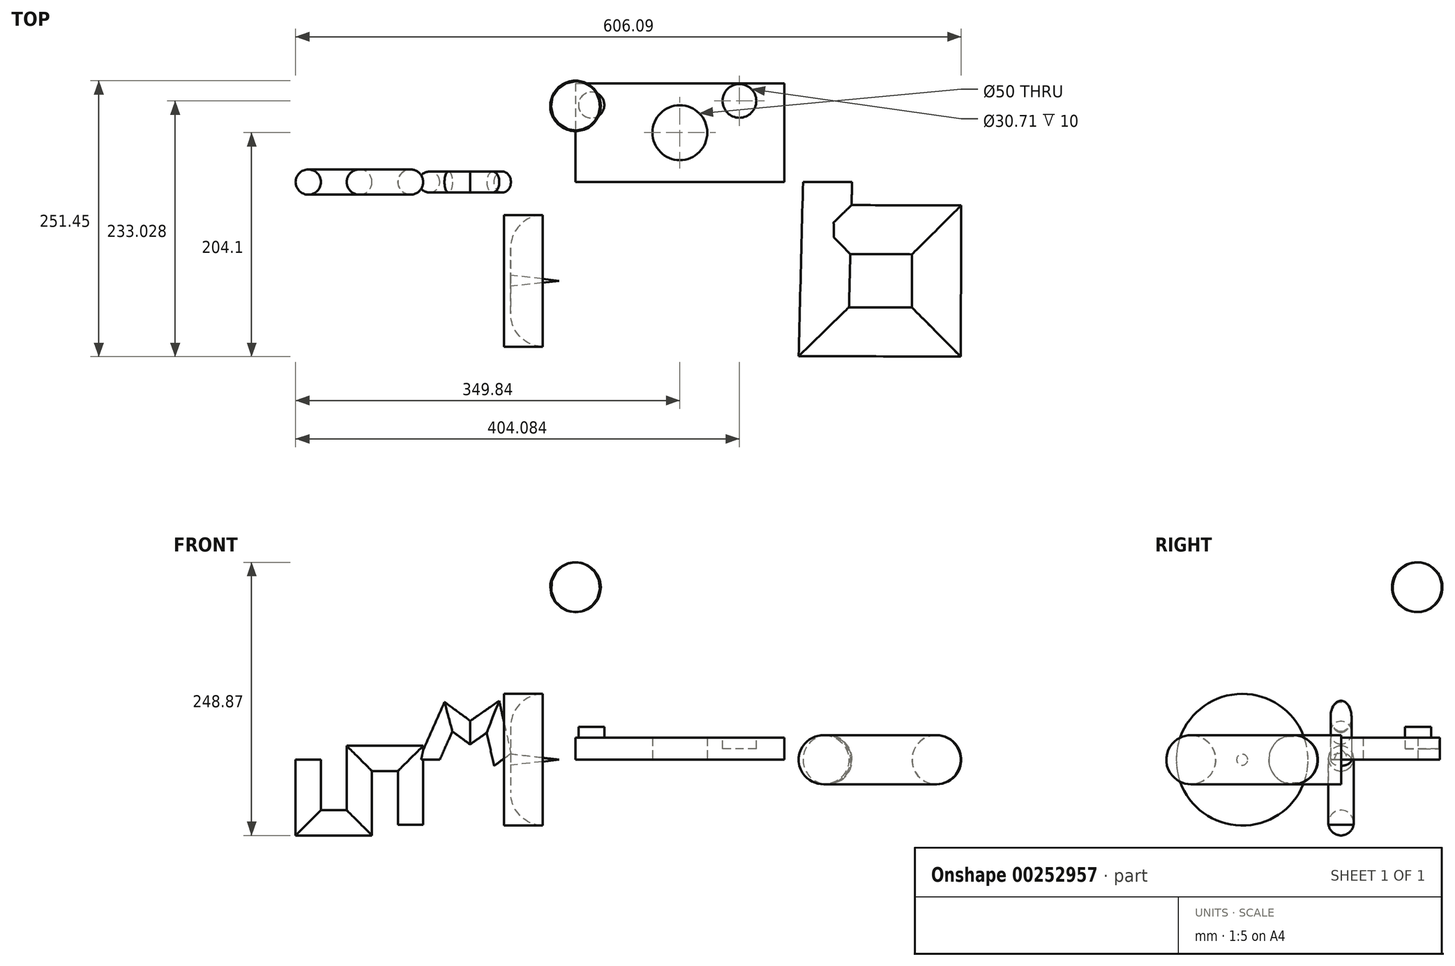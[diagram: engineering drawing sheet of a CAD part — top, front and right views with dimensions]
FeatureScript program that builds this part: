
annotation { "Feature Type Name" : "Feature", "Feature Type Description" : "" }
export const myFeature = defineFeature(function(context is Context, id is Id, definition is map)
    precondition{}
    {
        {
            var Q0;
            Q0=qCreatedBy(makeId("Top.planeOp"),FACE);
            var sketch = newSketch(context, id + "F0", { "sketchPlane" : qUnion([Q0])});
            skLineSegment(sketch, "E0.bottom", {"start": v(0, 90) * mm, "end": v(190, 90) * mm});
            skLineSegment(sketch, "E0.top", {"start": v(0, 0) * mm, "end": v(190, 0) * mm});
            skLineSegment(sketch, "E0.left", {"start": v(0, 90) * mm, "end": v(0, 0) * mm});
            skLineSegment(sketch, "E0.right", {"start": v(190, 90) * mm, "end": v(190, 0) * mm});
            skCircle(sketch, "E1", {"center": v(95, 45) * mm, "radius": 25 * mm});
            skSolve(sketch);
        }
        {
            var Q0;
            Q0 = qSketchRegion(id + "F0", true);
            extrude(context, id + "F1", {"entities" : qUnion([Q0]), "depth" : 20 * mm});
        }
        {
            var Q0;
            Q0=makeQuery(id+"F1.opExtrude","CAP_FACE",FACE,{"disambiguationData":[OSD([sQuery(id+"F0.wireOp",EDGE,"E0.bottom"),sQuery(id+"F0.wireOp",EDGE,"E0.top"),sQuery(id+"F0.wireOp",EDGE,"E0.left"),sQuery(id+"F0.wireOp",EDGE,"E0.right"),sQuery(id+"F0.wireOp",EDGE,"E1")])],"isStart":false});
            var sketch = newSketch(context, id + "F2", { "sketchPlane" : qUnion([Q0])});
            skCircle(sketch, "E2", {"center": v(149.24, 73.93) * mm, "radius": 15.36 * mm});
            skSolve(sketch);
        }
        {
            var Q0;
            Q0=makeQuery(id+"F2.imprint","IMPRINT",FACE,{"disambiguationData":[TD([[makeQuery(id+"F2.imprint","IMPRINT",EDGE,{"derivedFrom":sQuery(id+"F2.wireOp",EDGE,"E2")}),1.0]])]});
            extrude(context, id + "F3", {"entities" : qUnion([Q0]), "operationType" : NewBodyOperationType.REMOVE, "oppositeDirection" : true, "depth" : 10 * mm});
        }
        {
            var Q0;
            Q0=makeQuery(id+"F1.opExtrude","CAP_FACE",FACE,{"disambiguationData":[OSD([sQuery(id+"F0.wireOp",EDGE,"E0.bottom"),sQuery(id+"F0.wireOp",EDGE,"E0.top"),sQuery(id+"F0.wireOp",EDGE,"E0.left"),sQuery(id+"F0.wireOp",EDGE,"E0.right"),sQuery(id+"F0.wireOp",EDGE,"E1")])],"isStart":false});
            var sketch = newSketch(context, id + "F4", { "sketchPlane" : qUnion([Q0])});
            skCircle(sketch, "E3", {"center": v(14.47, 70.15) * mm, "radius": 11.77 * mm});
            skSolve(sketch);
        }
        {
            var Q0;
            Q0=makeQuery(id+"F4.imprint","IMPRINT",FACE,{"disambiguationData":[TD([[makeQuery(id+"F4.imprint","IMPRINT",EDGE,{"derivedFrom":sQuery(id+"F4.wireOp",EDGE,"E3")}),1.0]])]});
            extrude(context, id + "F5", {"entities" : qUnion([Q0]), "operationType" : NewBodyOperationType.ADD, "depth" : 10 * mm});
        }
        {
            var Q0;
            Q0=qCreatedBy(makeId("Top.planeOp"),FACE);
            var sketch = newSketch(context, id + "F6", { "sketchPlane" : qUnion([Q0])});
            skLineSegment(sketch, "E4", {"start": v(-65, -30) * mm, "end": v(-65, -90) * mm});
            skLineSegment(sketch, "E5", {"start": v(-65, -90) * mm, "end": v(-15, -90) * mm});
            skLineSegment(sketch, "E6", {"start": v(-15, -90) * mm, "end": v(-59, -84.98) * mm});
            skLineSegment(sketch, "E7", {"start": v(-59, -84.98) * mm, "end": v(-59, -59.98) * mm});
            skArc(sketch, "E8", {"start": v(-30, -30) * mm, "mid": v(-50.56, -39.13) * mm, "end": v(-59, -59.98) * mm});
            skLineSegment(sketch, "E9", {"start": v(-30, -30) * mm, "end": v(-65, -30) * mm});
            skSolve(sketch);
        }
        {
            var Q0;
            Q0 = qSketchRegion(id + "F6", true);
            var Q1;
            Q1=sQuery(id+"F6.wireOp",EDGE,"E5");
            revolve(context, id + "F7", {"entities" : qUnion([Q0]), "axis" : qUnion([Q1]), "revolveType" : RevolveType.FULL});
        }
        {
            var Q0;
            Q0=qCreatedBy(makeId("Right.planeOp"),FACE);
            var sketch = newSketch(context, id + "F8", { "sketchPlane" : qUnion([Q0])});
            skCircle(sketch, "E10", {"center": v(69.02, 157.2) * mm, "radius": 22.65 * mm});
            skLineSegment(sketch, "E11", {"start": v(69.7, 179.85) * mm, "end": v(69.02, 134.55) * mm});
            skSolve(sketch);
        }
        {
            var Q0;
            {var subQ0=sQuery(id+"F8.wireOp",EDGE,"E11");Q0=makeQuery(id+"F8.imprint","IMPRINT",FACE,{"disambiguationData":[TD([[makeQuery(id+"F8.imprint","IMPRINT",EDGE,{"derivedFrom":subQ0}),-1.0]])]});}
            var Q1;
            Q1=sQuery(id+"F8.wireOp",EDGE,"E11");
            revolve(context, id + "F9", {"entities" : qUnion([Q0]), "axis" : qUnion([Q1]), "revolveType" : RevolveType.FULL});
        }
        {
            var Q0;
            Q0=qCreatedBy(makeId("Top.planeOp"),FACE);
            var sketch = newSketch(context, id + "F10", { "sketchPlane" : qUnion([Q0])});
            skCircle(sketch, "E12", {"center": v(0, 0) * mm, "radius": 2.34 * mm});
            skCircle(sketch, "E13", {"center": v(-133.11, 0) * mm, "radius": 9.52 * mm});
            skSolve(sketch);
        }
        {
            var Q0;
            Q0=qCreatedBy(makeId("Front.planeOp"),FACE);
            var sketch = newSketch(context, id + "F11", { "sketchPlane" : qUnion([Q0])});
            skLineSegment(sketch, "E14", {"start": v(-132.97, 0) * mm, "end": v(-115.65, 38.95) * mm});
            skLineSegment(sketch, "E15", {"start": v(-115.65, 38.95) * mm, "end": v(-95.91, 24.5) * mm});
            skLineSegment(sketch, "E16", {"start": v(-95.91, 24.5) * mm, "end": v(-75.22, 38.95) * mm});
            skLineSegment(sketch, "E17", {"start": v(-75.22, 38.95) * mm, "end": v(-66.56, 0) * mm});
            skSolve(sketch);
        }
        {
            var Q0;
            Q0=makeQuery(id+"F10.imprint","IMPRINT",FACE,{"disambiguationData":[TD([[makeQuery(id+"F10.imprint","IMPRINT",EDGE,{"derivedFrom":sQuery(id+"F10.wireOp",EDGE,"E13")}),1.0]])]});
            var Q1;
            Q1=sQuery(id+"F11.wireOp",EDGE,"E14");
            var Q2;
            Q2=sQuery(id+"F11.wireOp",EDGE,"E15");
            var Q3;
            Q3=sQuery(id+"F11.wireOp",EDGE,"E16");
            var Q4;
            Q4=sQuery(id+"F11.wireOp",EDGE,"E17");
            sweep(context, id + "F12", {"profiles" : qUnion([Q0]), "path" : qUnion([Q1, Q2, Q3, Q4])});
        }
        {
            var Q0;
            Q0=qCreatedBy(makeId("Top.planeOp"),FACE);
            var sketch = newSketch(context, id + "F13", { "sketchPlane" : qUnion([Q0])});
            skCircle(sketch, "E18", {"center": v(-243.34, 0) * mm, "radius": 11.5 * mm});
            skSolve(sketch);
        }
        {
            var Q0;
            Q0=qCreatedBy(makeId("Front.planeOp"),FACE);
            var sketch = newSketch(context, id + "F14", { "sketchPlane" : qUnion([Q0])});
            skLineSegment(sketch, "E19", {"start": v(-244.48, 0) * mm, "end": v(-244.48, -58.65) * mm});
            skLineSegment(sketch, "E20", {"start": v(-244.48, -58.65) * mm, "end": v(-195.7, -58.65) * mm});
            skLineSegment(sketch, "E21", {"start": v(-195.7, -58.65) * mm, "end": v(-195.7, 0) * mm});
            skLineSegment(sketch, "E22", {"start": v(-195.7, 0) * mm, "end": v(-151.36, 0) * mm});
            skLineSegment(sketch, "E23", {"start": v(-151.36, 0) * mm, "end": v(-151.36, -59.39) * mm});
            skSolve(sketch);
        }
        {
            var Q0;
            Q0=makeQuery(id+"F13.imprint","IMPRINT",FACE,{"disambiguationData":[TD([[makeQuery(id+"F13.imprint","IMPRINT",EDGE,{"derivedFrom":sQuery(id+"F13.wireOp",EDGE,"E18")}),1.0]])]});
            var Q1;
            Q1=sQuery(id+"F14.wireOp",EDGE,"E19");
            var Q2;
            Q2=sQuery(id+"F14.wireOp",EDGE,"E20");
            var Q3;
            Q3=sQuery(id+"F14.wireOp",EDGE,"E21");
            var Q4;
            Q4=sQuery(id+"F14.wireOp",EDGE,"E22");
            var Q5;
            Q5=sQuery(id+"F14.wireOp",EDGE,"E23");
            sweep(context, id + "F15", {"operationType" : NewBodyOperationType.ADD, "profiles" : qUnion([Q0]), "path" : qUnion([Q1, Q2, Q3, Q4, Q5])});
        }
        {
            var Q0;
            Q0=qCreatedBy(makeId("Front.planeOp"),FACE);
            var sketch = newSketch(context, id + "F16", { "sketchPlane" : qUnion([Q0])});
            skCircle(sketch, "E24", {"center": v(229.53, 0) * mm, "radius": 22.34 * mm});
            skCircle(sketch, "E25", {"center": v(337.8, 160.2) * mm, "radius": 37.32 * mm});
            skSolve(sketch);
        }
        {
            var Q0;
            Q0=qCreatedBy(makeId("Top.planeOp"),FACE);
            var sketch = newSketch(context, id + "F17", { "sketchPlane" : qUnion([Q0])});
            skLineSegment(sketch, "E26", {"start": v(228.72, 0) * mm, "end": v(225.28, -137.18) * mm});
            skLineSegment(sketch, "E27", {"start": v(225.28, -137.18) * mm, "end": v(329.35, -137.51) * mm});
            skLineSegment(sketch, "E28", {"start": v(329.35, -137.51) * mm, "end": v(329.65, -42.79) * mm});
            skLineSegment(sketch, "E29", {"start": v(329.65, -42.79) * mm, "end": v(235.19, -42.49) * mm});
            skSolve(sketch);
        }
        {
            var Q0;
            Q0=makeQuery(id+"F16.imprint","IMPRINT",FACE,{"disambiguationData":[TD([[makeQuery(id+"F16.imprint","IMPRINT",EDGE,{"derivedFrom":sQuery(id+"F16.wireOp",EDGE,"E24")}),1.0]])]});
            var Q1;
            Q1=sQuery(id+"F17.wireOp",EDGE,"E26");
            var Q2;
            Q2=sQuery(id+"F17.wireOp",EDGE,"E27");
            var Q3;
            Q3=sQuery(id+"F17.wireOp",EDGE,"E28");
            var Q4;
            Q4=sQuery(id+"F17.wireOp",EDGE,"E29");
            sweep(context, id + "F18", {"profiles" : qUnion([Q0]), "path" : qUnion([Q1, Q2, Q3, Q4])});
        }
    });
